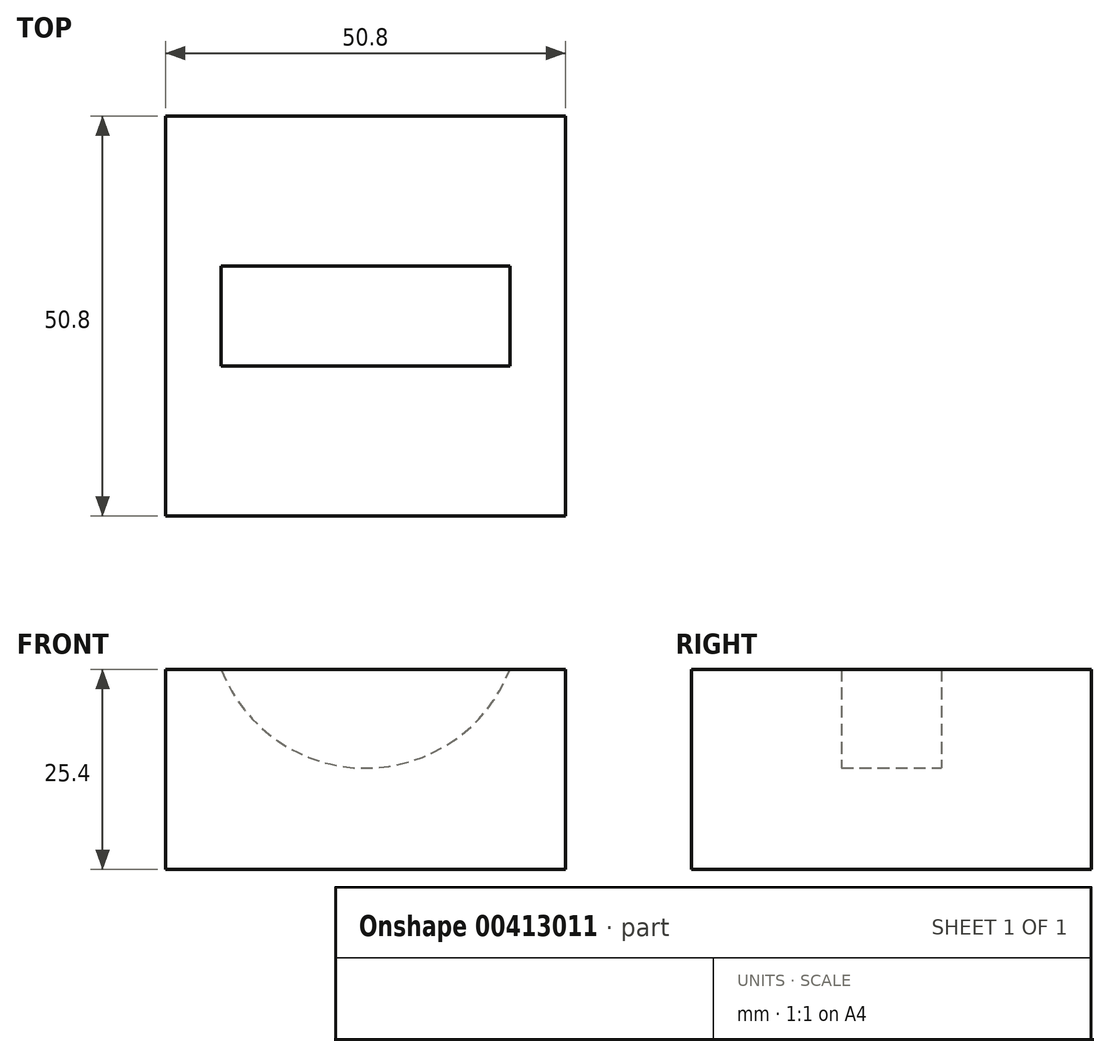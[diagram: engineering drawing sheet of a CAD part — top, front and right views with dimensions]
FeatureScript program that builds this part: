
annotation { "Feature Type Name" : "Feature", "Feature Type Description" : "" }
export const myFeature = defineFeature(function(context is Context, id is Id, definition is map)
    precondition{}
    {
        {
            var Q0;
            Q0=qCreatedBy(makeId("Front.planeOp"),FACE);
            var sketch = newSketch(context, id + "F0", { "sketchPlane" : qUnion([Q0])});
            skLineSegment(sketch, "E0.bottom", {"start": v(25.4, -12.7) * mm, "end": v(-25.4, -12.7) * mm});
            skLineSegment(sketch, "E0.top", {"start": v(25.4, 12.7) * mm, "end": v(-25.4, 12.7) * mm});
            skLineSegment(sketch, "E0.left", {"start": v(25.4, -12.7) * mm, "end": v(25.4, 12.7) * mm});
            skLineSegment(sketch, "E0.right", {"start": v(-25.4, -12.7) * mm, "end": v(-25.4, 12.7) * mm});
            skPoint(sketch, "E0.middle", {"position": v(0, 0) * mm});
            skSolve(sketch);
        }
        {
            var Q0;
            Q0=qCreatedBy(makeId("Front.planeOp"),FACE);
            var sketch = newSketch(context, id + "F1", { "sketchPlane" : qUnion([Q0])});
            skArc(sketch, "E1", {"start": v(-18.56, 13.31) * mm, "mid": v(0, 0.16) * mm, "end": v(18.56, 13.31) * mm});
            skLineSegment(sketch, "E2", {"start": v(-18.56, 13.31) * mm, "end": v(18.56, 13.31) * mm});
            skSolve(sketch);
        }
        {
            var Q0;
            Q0 = qSketchRegion(id + "F0", true);
            extrude(context, id + "F2", {"entities" : qUnion([Q0]), "endBound" : BoundingType.SYMMETRIC, "depth" : 50.8 * mm});
        }
        {
            var Q0;
            Q0 = qSketchRegion(id + "F1", true);
            extrude(context, id + "F3", {"entities" : qUnion([Q0]), "operationType" : NewBodyOperationType.REMOVE, "endBound" : BoundingType.SYMMETRIC, "depth" : 12.7 * mm});
        }
    });
